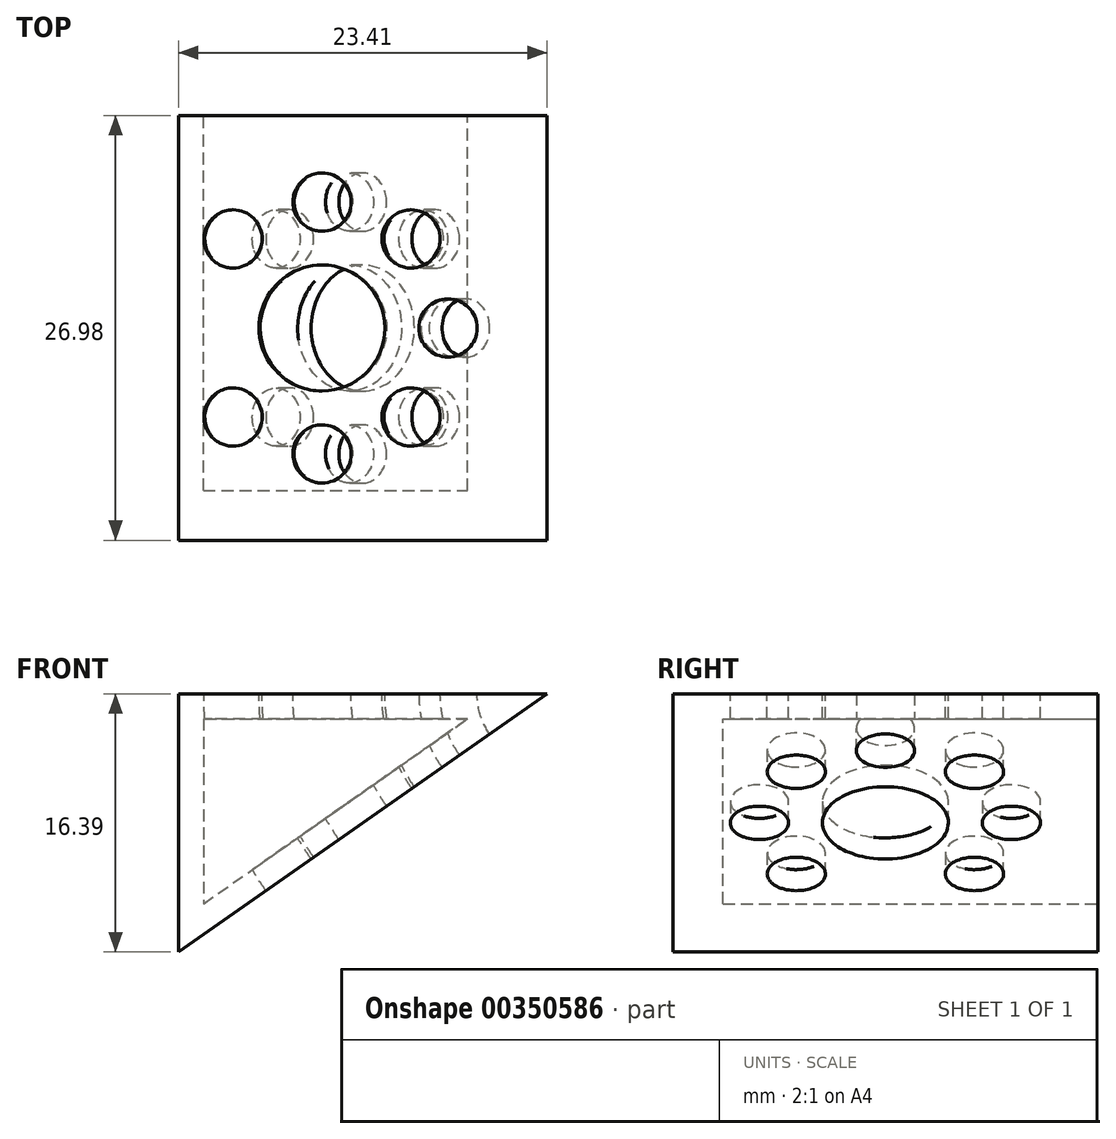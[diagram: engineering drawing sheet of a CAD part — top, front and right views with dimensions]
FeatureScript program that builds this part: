
annotation { "Feature Type Name" : "Feature", "Feature Type Description" : "" }
export const myFeature = defineFeature(function(context is Context, id is Id, definition is map)
    precondition{}
    {
        {
            var Q0;
            Q0=qCreatedBy(makeId("Top.planeOp"),FACE);
            var sketch = newSketch(context, id + "F0", { "sketchPlane" : qUnion([Q0])});
            skLineSegment(sketch, "E0.bottom", {"start": v(-14.29, 13.5) * mm, "end": v(14.29, 13.5) * mm});
            skLineSegment(sketch, "E0.top", {"start": v(-14.29, -13.5) * mm, "end": v(14.29, -13.5) * mm});
            skLineSegment(sketch, "E0.left", {"start": v(-14.29, 13.5) * mm, "end": v(-14.29, -13.5) * mm});
            skLineSegment(sketch, "E0.right", {"start": v(14.29, 13.5) * mm, "end": v(14.29, -13.5) * mm});
            skPoint(sketch, "E0.middle", {"position": v(0, 0) * mm});
            skCircle(sketch, "E1", {"center": v(0, 0) * mm, "radius": 4 * mm});
            skCircle(sketch, "E2", {"center": v(0, 8) * mm, "radius": 1.85 * mm});
            skCircle(sketch, "E3.1.0", {"center": v(-5.66, 5.66) * mm, "radius": 1.85 * mm});
            skCircle(sketch, "E3.3.0", {"center": v(-5.66, -5.66) * mm, "radius": 1.85 * mm});
            skCircle(sketch, "E3.4.0", {"center": v(0, -8) * mm, "radius": 1.85 * mm});
            skCircle(sketch, "E3.5.0", {"center": v(5.66, -5.66) * mm, "radius": 1.85 * mm});
            skCircle(sketch, "E3.6.0", {"center": v(8, 0) * mm, "radius": 1.85 * mm});
            skCircle(sketch, "E3.7.0", {"center": v(5.66, 5.66) * mm, "radius": 1.85 * mm});
            skSolve(sketch);
        }
        {
            var Q0;
            Q0=makeQuery(id+"F0.imprint","IMPRINT",FACE,{"disambiguationData":[TD([[makeQuery(id+"F0.imprint","IMPRINT",EDGE,{"derivedFrom":sQuery(id+"F0.wireOp",EDGE,"E0.bottom")}),-1.0]])]});
            var Q1;
            Q1=sQuery(id+"F0.wireOp",EDGE,"E0.right");
            revolve(context, id + "F1", {"entities" : qUnion([Q0]), "axis" : qUnion([Q1]), "revolveType" : RevolveType.ONE_DIRECTION, "angle" : 35 * degree});
        }
        {
            var Q0;
            Q0=makeQuery(id+"F1.opRevolve","SWEPT_FACE",FACE,{"disambiguationData":[OSD([sQuery(id+"F0.wireOp",EDGE,"E0.bottom")])]});
            var sketch = newSketch(context, id + "F2", { "sketchPlane" : qUnion([Q0])});
            skLineSegment(sketch, "E4", {"start": v(9.12, -16.39) * mm, "end": v(9.12, 0) * mm});
            skLineSegment(sketch, "E5", {"start": v(9.12, -1.59) * mm, "end": v(-12.02, -1.59) * mm});
            skLineSegment(sketch, "E6", {"start": v(7.53, -1.59) * mm, "end": v(7.53, -15.28) * mm});
            skLineSegment(sketch, "E7", {"start": v(7.53, -13.34) * mm, "end": v(-9.25, -1.59) * mm});
            skSolve(sketch);
        }
        {
            var Q0;
            {var subQ0=sQuery(id+"F2.wireOp",EDGE,"E4");Q0=makeQuery(id+"F2.imprint","IMPRINT",FACE,{"disambiguationData":[TD([[makeQuery(id+"F2.imprint","IMPRINT",EDGE,{"derivedFrom":subQ0}),-1.0]])]});}
            extrude(context, id + "F3", {"entities" : qUnion([Q0]), "operationType" : NewBodyOperationType.REMOVE, "oppositeDirection" : true, "depth" : 76.2 * mm});
        }
        {
            var Q0;
            {var subQ3=sQuery(id+"F2.wireOp",EDGE,"E7");Q0=makeQuery(id+"F2.imprint","IMPRINT",FACE,{"disambiguationData":[TD([[makeQuery(id+"F2.imprint","IMPRINT",EDGE,{"derivedFrom":subQ3}),-1.0]])]});}
            extrude(context, id + "F4", {"entities" : qUnion([Q0]), "operationType" : NewBodyOperationType.REMOVE, "oppositeDirection" : true, "depth" : 23.8 * mm});
        }
    });
